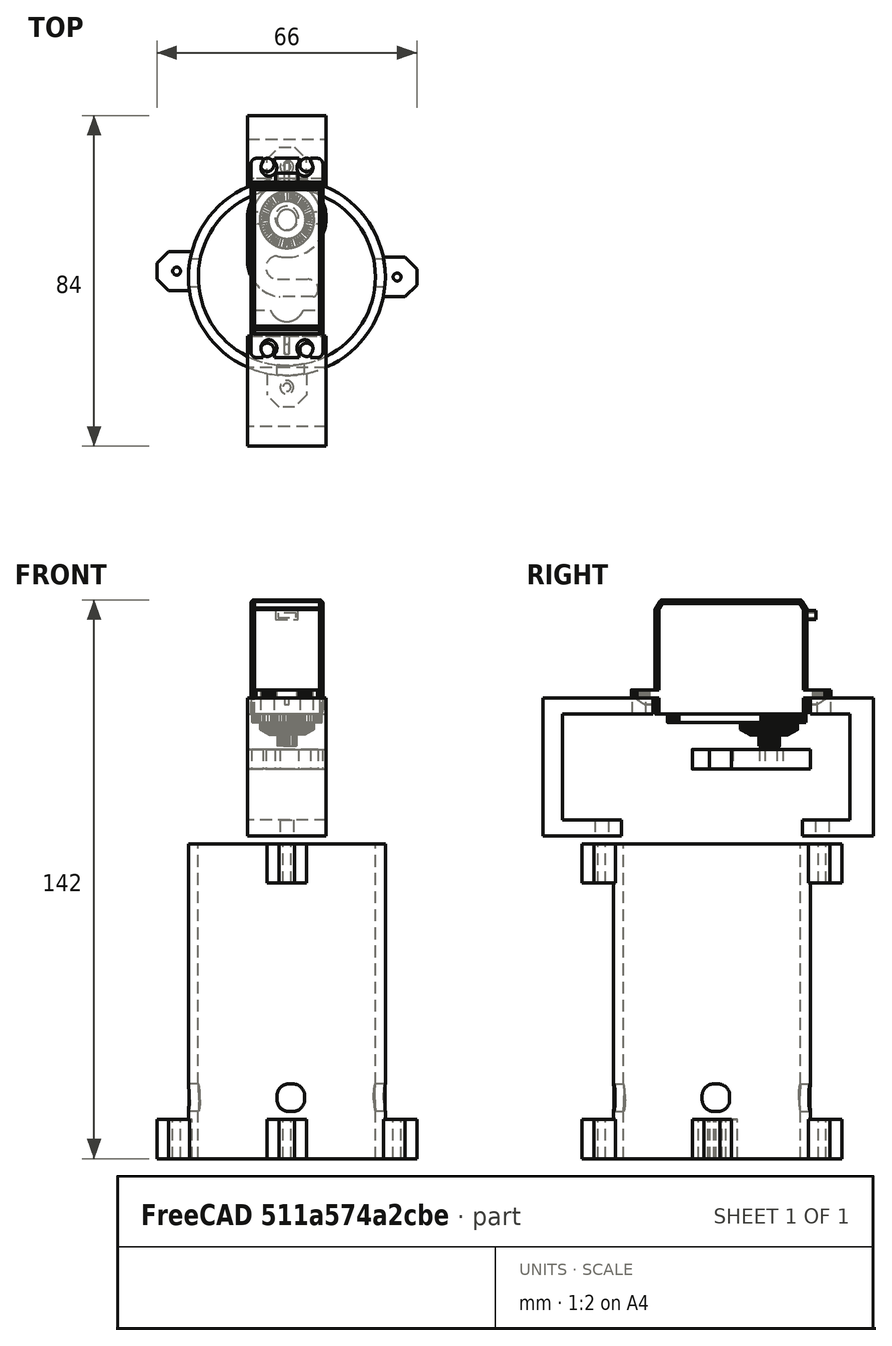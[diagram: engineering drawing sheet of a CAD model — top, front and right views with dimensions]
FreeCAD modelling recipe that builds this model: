
FCSTD DOCUMENT  (FreeCAD 0.15R4671 (Git))
Label: Funny action
License: All rights reserved
LicenseURL: http://fr.wikipedia.org/wiki/<copyright redacted>
objects: Part::Cut×13, Part::Box×10, Part::Cylinder×10, Part::Chamfer×6, Part::MultiFuse×6, Part::Part2DObjectPython×5, Part::Extrusion×4, Part::Fillet×2, Mesh::Feature×1, Part::FeaturePython×1, Part::Feature×1
note: 58 computed .brp shape members not serialized (recipe doc carries the construction recipe); baked Part::Feature solids carry a one-line shape summary decoded from their .brp

FEATURE [Part::Box] Box  label="Cube"
  Height = 7
  Length = 7
  Placement = pos=(-2.5,-60,12) rot=(0,0,1;0rad)
  Width = 120
FEATURE [Part::Fillet] Fillet001
  Base = -> Box
  Edges = 4 edges r=3: [Edge2,Edge4,Edge6,Edge8]
FEATURE [Part::Cylinder] Cylinder008  label="Cylindre008"
  Angle = 360
  Height = 80
  Radius = 25
FEATURE [Part::Cylinder] Cylinder009  label="Cylindre009"
  Angle = 360
  Height = 80
  Radius = 22.5
FEATURE [Part::Cut] Cut008
  Base = -> Cylinder008
  Tool = -> Cylinder009
FEATURE [Part::Box] Box001  label="Cube001"
  Height = 7
  Length = 7
  Placement = pos=(60,-2.5,12) rot=(0,0,1;1.5708rad)
  Width = 120
FEATURE [Part::Fillet] Fillet
  Base = -> Box001
  Edges = 4 edges r=3: [Edge2,Edge4,Edge6,Edge8]
FEATURE [Part::Cut] Cut
  Base = -> Cut008
  Tool = -> Fillet001
FEATURE [Part::Cut] Cut009  label="base"
  Base = -> Cut
  Tool = -> Fillet
FEATURE [Part::Cylinder] Cylinder015  label="Cylindre"
  Angle = 360
  Height = 10
  Placement = pos=(5,5,0) rot=(0,0,1;0rad)
  Radius = 1
FEATURE [Part::Box] Box002  label="Cube002"
  Height = 10
  Length = 10
  Width = 10
FEATURE [Part::Cut] Cut014  label="visse servo 1"
  Base = -> Box002
  Placement = pos=(-5,48,70) rot=(0,0,1;0rad)
  Tool = -> Cylinder015
FEATURE [Part::Chamfer] Chamfer  label="visse servo 003"
  Base = -> Cut014
  Edges = 2 edges r=3: [Edge3,Edge12]
  Placement = pos=(0,-25,0) rot=(0,0,1;0rad)
FEATURE [Part::Cylinder] Cylinder  label="Cylindre017"
  Angle = 360
  Height = 10
  Placement = pos=(5,5,0) rot=(0,0,1;0rad)
  Radius = 1
FEATURE [Part::Box] Box004  label="Cube004"
  Height = 10
  Length = 10
  Width = 10
FEATURE [Part::Cut] Cut015  label="visse servo 002"
  Base = -> Box004
  Placement = pos=(-5,48,70) rot=(0,0,1;0rad)
  Tool = -> Cylinder
FEATURE [Part::Chamfer] Chamfer001
  Base = -> Cut015
  Edges = 2 edges r=3: [Edge3,Edge12]
  Placement = pos=(0,25,0) rot=(0,0,1;3.14159rad)
FEATURE [Part::Cylinder] Cylinder017  label="Cylindre018"
  Angle = 360
  Height = 10
  Placement = pos=(5,5,0) rot=(0,0,1;0rad)
  Radius = 1
FEATURE [Part::Box] Box005  label="Cube005"
  Height = 10
  Length = 10
  Width = 10
FEATURE [Part::Cut] Cut016  label="visse servo 004"
  Base = -> Box005
  Placement = pos=(-5,48,70) rot=(0,0,1;0rad)
  Tool = -> Cylinder017
FEATURE [Part::Chamfer] Chamfer002
  Base = -> Cut016
  Edges = 2 edges r=3: [Edge3,Edge12]
  Placement = pos=(0,-25,-70) rot=(0,0,1;0rad)
FEATURE [Part::Cylinder] Cylinder018  label="Cylindre019"
  Angle = 360
  Height = 10
  Placement = pos=(5,5,0) rot=(0,0,1;0rad)
  Radius = 1
FEATURE [Part::Box] Box006  label="Cube006"
  Height = 10
  Length = 10
  Width = 10
FEATURE [Part::Cut] Cut017  label="visse servo 005"
  Base = -> Box006
  Placement = pos=(-5,48,70) rot=(0,0,1;0rad)
  Tool = -> Cylinder018
FEATURE [Part::Chamfer] Chamfer003
  Base = -> Cut017
  Edges = 2 edges r=3: [Edge3,Edge12]
  Placement = pos=(25,1.5,-70) rot=(0,0,1;1.5708rad)
FEATURE [Part::Cylinder] Cylinder019  label="Cylindre020"
  Angle = 360
  Height = 10
  Placement = pos=(5,5,0) rot=(0,0,1;0rad)
  Radius = 1
FEATURE [Part::Box] Box007  label="Cube007"
  Height = 10
  Length = 10
  Width = 10
FEATURE [Part::Cut] Cut018  label="visse servo 006"
  Base = -> Box007
  Placement = pos=(-5,48,70) rot=(0,0,1;0rad)
  Tool = -> Cylinder019
FEATURE [Part::Chamfer] Chamfer004
  Base = -> Cut018
  Edges = 2 edges r=3: [Edge3,Edge12]
  Placement = pos=(-25,0,-70) rot=(0,0,-1;1.5708rad)
FEATURE [Part::Cylinder] Cylinder020  label="Cylindre021"
  Angle = 360
  Height = 10
  Placement = pos=(5,5,0) rot=(0,0,1;0rad)
  Radius = 1
FEATURE [Part::Box] Box008  label="Cube008"
  Height = 10
  Length = 10
  Width = 10
FEATURE [Part::Cut] Cut019  label="visse servo 007"
  Base = -> Box008
  Placement = pos=(-5,48,70) rot=(0,0,1;0rad)
  Tool = -> Cylinder020
FEATURE [Part::Chamfer] Chamfer005
  Base = -> Cut019
  Edges = 2 edges r=3: [Edge3,Edge12]
  Placement = pos=(0,25,-70) rot=(0,0,1;3.14159rad)
FEATURE [Part::MultiFuse] Fusion  label="visses"
  Shapes = -> [Chamfer001,Chamfer004,Chamfer,Chamfer002,Chamfer003,Chamfer005]
FEATURE [Part::MultiFuse] Fusion001  label="propulseur"
  Placement = pos=(0,0,6) rot=(0,0,1;0rad)
  Shapes = -> [Cut009,Fusion]
FEATURE [Part::Part2DObjectPython] Rectangle002  # Draft 2D object (typed FeaturePython)
  ChamferSize = 0
  FilletRadius = 0
  Height = 6
  Length = 20
  MakeFace = true
  Placement = pos=(-10,27,0) rot=(0,0,1;0rad)
FEATURE [Part::Part2DObjectPython] Rectangle003  # Draft 2D object (typed FeaturePython)
  ChamferSize = 0
  FilletRadius = 0
  Height = -20
  Length = 20
  MakeFace = true
  Placement = pos=(-10,-25,0) rot=(0,0,1;0rad)
FEATURE [Part::Extrusion] Extrude
  Base = -> Rectangle003
  Dir = (0,0,35)
  Solid = true
FEATURE [Part::Extrusion] Extrude002
  Base = -> Rectangle002
  Dir = (0,0,35)
  Placement = pos=(0,0,-20) rot=(0,0,1;0rad)
  Solid = false
FEATURE [Part::Box] Box009  label="Cube009"
  Height = 27
  Length = 20
  Placement = pos=(-10,-40,4) rot=(0,0,1;0rad)
  Width = 15
FEATURE [Part::Cut] Cut023
  Base = -> Extrude
  Placement = pos=(0,0,-20) rot=(0,0,1;0rad)
  Tool = -> Box009
FEATURE [Part::Box] Box010  label="Cube010"
  Height = 4
  Length = 20
  Placement = pos=(-10,15,1) rot=(0,0,1;0rad)
  Width = 18
FEATURE [Part::Cylinder] Cylinder021  label="Cylindre022"
  Angle = 360
  Height = 10
  Placement = pos=(0,-30,8) rot=(0,0,1;0rad)
  Radius = 1.7
FEATURE [Part::Cut] Cut024
  Base = -> Cut023
  Tool = -> Cylinder021
FEATURE [Part::Cylinder] Cylinder022  label="Cylindre023"
  Angle = 360
  Height = 10
  Placement = pos=(0,20,-2) rot=(0,0,1;0rad)
  Radius = 1.7
FEATURE [Part::Cut] Cut025
  Base = -> Box010
  Placement = pos=(0,0,10) rot=(0,0,1;0rad)
  Tool = -> Cylinder022
FEATURE [Part::Part2DObjectPython] Circle002  # Draft 2D object (typed FeaturePython)
  FirstAngle = 0
  LastAngle = 0
  MakeFace = true
  Placement = pos=(-5,21.5,0) rot=(0,0,1;0rad)
  Radius = 1.7
FEATURE [Part::Part2DObjectPython] Circle003  # Draft 2D object (typed FeaturePython)
  FirstAngle = 0
  LastAngle = 0
  MakeFace = true
  Placement = pos=(5,21.5,0) rot=(0,0,1;0rad)
  Radius = 1.7
FEATURE [Part::MultiFuse] Fusion004
  Placement = pos=(0,-43,0) rot=(0,0,1;0rad)
  Shapes = -> [Circle003,Circle002]
FEATURE [Part::Part2DObjectPython] Rectangle  # Draft 2D object (typed FeaturePython)
  ChamferSize = 0
  FilletRadius = 0
  Height = 15
  Length = 20
  MakeFace = true
  Placement = pos=(-10,-25,0) rot=(0,0,1;0rad)
FEATURE [Part::Cut] Cut026
  Base = -> Rectangle
  Tool = -> Fusion004
FEATURE [Part::Extrusion] Extrude003
  Base = -> Cut026
  Dir = (0,0,4)
  Placement = pos=(0,-42,-20) rot=(0,0,1;3.14159rad)
  Solid = false
FEATURE [Part::Extrusion] Extrude004
  Base = -> Cut026
  Dir = (0,0,4)
  Placement = pos=(0,42,-20) rot=(0,0,1;0rad)
  Solid = false
FEATURE [Part::MultiFuse] Fusion005  label="fixation  servo large"
  Placement = pos=(0,2,0) rot=(0,0,1;0rad)
  Shapes = -> [Extrude003,Cut024]
FEATURE [Part::MultiFuse] Fusion006  label="fixation servo court"
  Placement = pos=(0,8,0) rot=(0,0,1;0rad)
  Shapes = -> [Cut025,Extrude002,Extrude004]
FEATURE [Part::MultiFuse] Fusion007  label="fixation"
  Placement = pos=(0,0,103) rot=(0,1,0;3.14159rad)
  Shapes = -> [Fusion006,Fusion005]
FEATURE [Mesh::Feature] propulseurV3_  label="propulseurV3."
  Placement = pos=(0,0,40) rot=(0,0,1;0rad)
FEATURE [Part::FeaturePython] Clone  label="Servo"  # WARN: FeaturePython — macro-defined, semantics opaque (R4)
  Placement = pos=(0,14.5,-932) rot=(0,0,1;3.14159rad)
  Scale = (9,9.5,9)
FEATURE [Part::Feature] Part__Feature  label="acroche"
  Placement = pos=(0,10,105) rot=(0,0,1;4.71239rad)
  shape: bbox 20 x 30 x 5 mm, 20 faces (baked)
